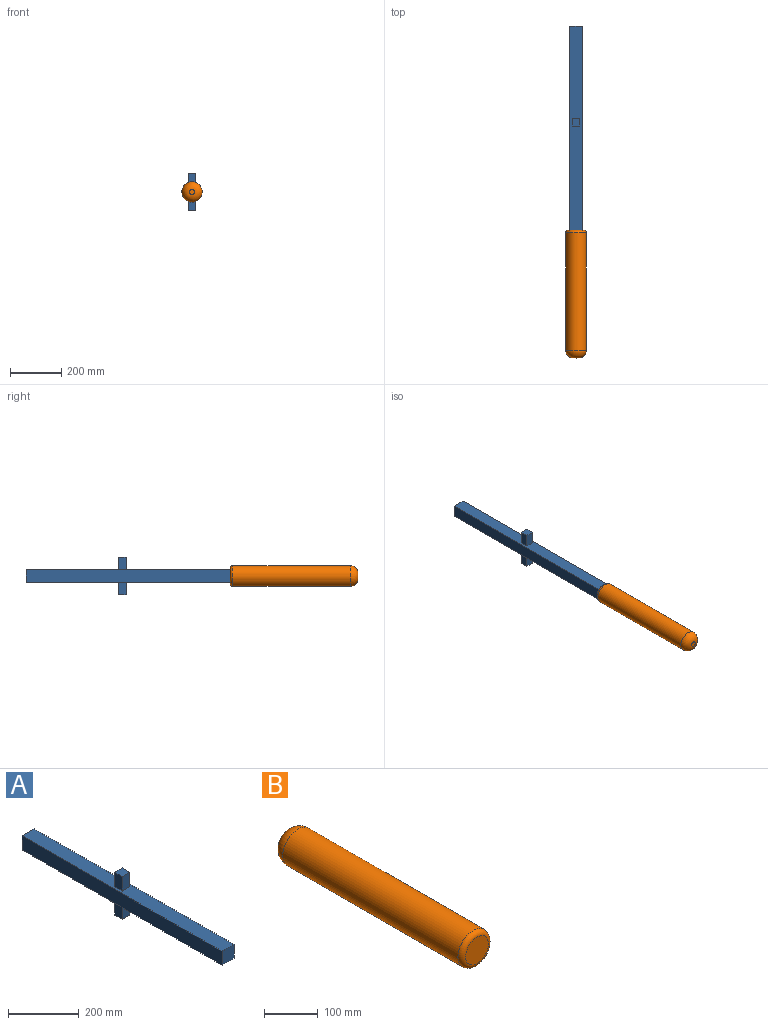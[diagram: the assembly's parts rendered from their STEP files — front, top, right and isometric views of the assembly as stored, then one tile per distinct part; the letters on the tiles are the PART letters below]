
ASSEMBLY  parts=2 mates=1
PART A: 16 faces, bbox 48x800x148 mm
  f0: plane 800x48mm, normal (0,0,1), area 37500mm2, adj f1,f2,f4,f5,f6,f7,f8,f9
  f1: plane 800x48mm, normal (1,0,0), area 38400mm2, adj f0,f3,f4,f5
  f2: plane 800x48mm, normal (-1,0,0), area 38400mm2, adj f0,f3,f4,f5
  f3: plane 800x48mm, normal (0,0,-1), area 37500mm2, adj f1,f2,f4,f5,f11,f12,f13,f14
  f4: plane 48x48mm, normal (0,1,0), area 2304mm2, adj f0,f1,f2,f3
  f5: plane 48x48mm, normal (0,-1,0), area 2304mm2, adj f0,f1,f2,f3
  f6: plane 50x30mm, normal (0,1,0), area 1500mm2, adj f0,f7,f9,f10
  f7: plane 50x30mm, normal (-1,0,0), area 1500mm2, adj f0,f6,f8,f10
  f8: plane 50x30mm, normal (0,-1,0), area 1500mm2, adj f0,f7,f9,f10
  f9: plane 50x30mm, normal (1,0,0), area 1500mm2, adj f0,f6,f8,f10
  f10: plane 30x30mm, normal (0,0,1), area 900mm2, adj f6,f7,f8,f9
  f11: plane 50x30mm, normal (0,-1,0), area 1500mm2, adj f3,f12,f14,f15
  f12: plane 50x30mm, normal (-1,0,0), area 1500mm2, adj f3,f11,f13,f15
  f13: plane 50x30mm, normal (0,1,0), area 1500mm2, adj f3,f12,f14,f15
  f14: plane 50x30mm, normal (1,0,0), area 1500mm2, adj f3,f11,f13,f15
  f15: plane 30x30mm, normal (0,0,-1), area 900mm2, adj f11,f12,f13,f14
PART B: 5 faces, bbox 86.6x500x86.6 mm
  f0: cylinder r=40mm len=460mm, axis (0,-1,0), area 115610.6mm2, adj f3,f4
  f1: plane 20x20mm, normal (0,1,0), area 314.2mm2, adj f3
  f2: plane 60x60mm, normal (0,-1,0), area 2827.4mm2, adj f4
  f3: torus R=10mm, axis (0,-1,0), area 8615.7mm2, adj f0,f1
  f4: torus R=30mm, axis (0,-1,0), area 3589.2mm2, adj f0,f2
PLACE A t=(0,500,0)mm
PLACE B rot(axis=(0,0,1),180deg) t=(0,500,0)mm
MATE fastened A.f5 <-> B.f0  axis (0,-1,0) through (0,500,0)mm
